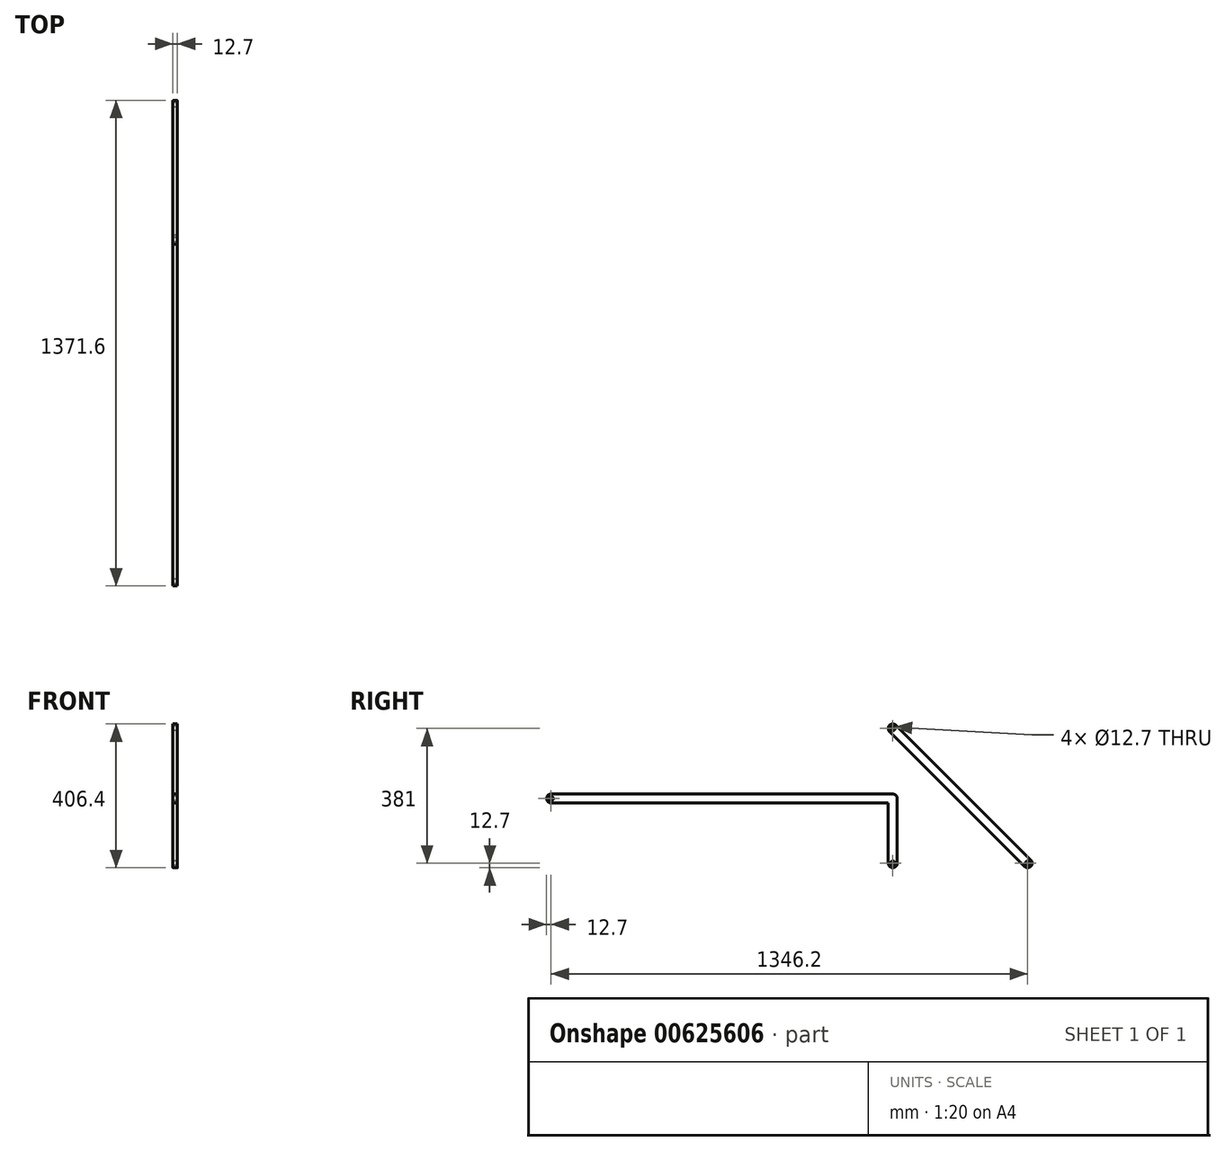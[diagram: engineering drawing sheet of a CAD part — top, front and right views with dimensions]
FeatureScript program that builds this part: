
annotation { "Feature Type Name" : "Feature", "Feature Type Description" : "" }
export const myFeature = defineFeature(function(context is Context, id is Id, definition is map)
    precondition{}
    {
        {
            var Q0;
            Q0=qCreatedBy(makeId("Right.planeOp"),FACE);
            var sketch = newSketch(context, id + "F0", { "sketchPlane" : qUnion([Q0])});
            skLineSegment(sketch, "E0", {"start": v(0, 0) * mm, "end": v(0, -381) * mm, "construction": true});
            skLineSegment(sketch, "E1", {"start": v(0, -381) * mm, "end": v(381, -381) * mm, "construction": true});
            skLineSegment(sketch, "E2", {"start": v(381, -381) * mm, "end": v(0, 0) * mm, "construction": true});
            skCircle(sketch, "E3", {"center": v(0, 0) * mm, "radius": 6.35 * mm});
            skCircle(sketch, "E4", {"center": v(381, -381) * mm, "radius": 6.35 * mm});
            skCircle(sketch, "E5", {"center": v(0, -381) * mm, "radius": 6.35 * mm});
            skArc(sketch, "E6.0.startCap", {"start": v(389.98, -372.02) * mm, "mid": v(389.98, -389.98) * mm, "end": v(372.02, -389.98) * mm});
            skArc(sketch, "E6.0.endCap", {"start": v(-8.98, -8.98) * mm, "mid": v(-8.98, 8.98) * mm, "end": v(8.98, 8.98) * mm});
            skLineSegment(sketch, "E6.0.left", {"start": v(372.02, -389.98) * mm, "end": v(-8.98, -8.98) * mm});
            skLineSegment(sketch, "E6.0.right", {"start": v(389.98, -372.02) * mm, "end": v(8.98, 8.98) * mm});
            skArc(sketch, "E6.1.startCap", {"start": v(-12.7, 0) * mm, "mid": v(0, 12.7) * mm, "end": v(12.7, 0) * mm, "construction": true});
            skArc(sketch, "E6.1.endCap", {"start": v(12.7, -381) * mm, "mid": v(0, -393.7) * mm, "end": v(-12.7, -381) * mm});
            skLineSegment(sketch, "E6.1.left", {"start": v(12.7, 0) * mm, "end": v(12.7, -381) * mm});
            skLineSegment(sketch, "E6.1.right", {"start": v(-12.7, 0) * mm, "end": v(-12.7, -381) * mm});
            skArc(sketch, "E6.2.startCap", {"start": v(0, -393.7) * mm, "mid": v(-12.7, -381) * mm, "end": v(0, -368.3) * mm});
            skArc(sketch, "E6.2.endCap", {"start": v(381, -368.3) * mm, "mid": v(393.7, -381) * mm, "end": v(381, -393.7) * mm});
            skLineSegment(sketch, "E6.2.left", {"start": v(0, -368.3) * mm, "end": v(381, -368.3) * mm});
            skLineSegment(sketch, "E6.2.right", {"start": v(0, -393.7) * mm, "end": v(381, -393.7) * mm});
            skLineSegment(sketch, "E7", {"start": v(0, -198.12) * mm, "end": v(-965.2, -198.12) * mm, "construction": true});
            skCircle(sketch, "E8", {"center": v(-965.2, -198.12) * mm, "radius": 6.35 * mm});
            skArc(sketch, "E9.0.startCap", {"start": v(0, -185.42) * mm, "mid": v(12.7, -198.12) * mm, "end": v(0, -210.82) * mm});
            skArc(sketch, "E9.0.endCap", {"start": v(-965.2, -210.82) * mm, "mid": v(-977.9, -198.12) * mm, "end": v(-965.2, -185.42) * mm});
            skLineSegment(sketch, "E9.0.left", {"start": v(0, -210.82) * mm, "end": v(-965.2, -210.82) * mm});
            skLineSegment(sketch, "E9.0.right", {"start": v(0, -185.42) * mm, "end": v(-965.2, -185.42) * mm});
            skSolve(sketch);
        }
        {
            var Q0;
            {var subQ5=sQuery(id+"F0.wireOp",EDGE,"E6.1.right");Q0=makeQuery(id+"F0.imprint","IMPRINT",FACE,{"disambiguationData":[TD([[makeQuery(id+"F0.imprint","IMPRINT",EDGE,{"derivedFrom":subQ5}),1.0]])]});}
            var Q1;
            {var subQ5=sQuery(id+"F0.wireOp",EDGE,"E6.0.startCap");Q1=makeQuery(id+"F0.imprint","IMPRINT",FACE,{"disambiguationData":[TD([[makeQuery(id+"F0.imprint","IMPRINT",EDGE,{"derivedFrom":subQ5}),1.0]])]});}
            var Q2;
            Q2=makeQuery(id+"F0.imprint","IMPRINT",FACE,{"disambiguationData":[TD([[makeQuery(id+"F0.imprint","IMPRINT",EDGE,{"derivedFrom":sQuery(id+"F0.wireOp",EDGE,"E4")}),-1.0]])]});
            var Q3;
            Q3=makeQuery(id+"F0.imprint","IMPRINT",FACE,{"disambiguationData":[TD([[makeQuery(id+"F0.imprint","IMPRINT",EDGE,{"derivedFrom":sQuery(id+"F0.wireOp",EDGE,"E3")}),-1.0]])]});
            var Q4;
            Q4=makeQuery(id+"F0.imprint","IMPRINT",FACE,{"disambiguationData":[TD([[makeQuery(id+"F0.imprint","IMPRINT",EDGE,{"derivedFrom":sQuery(id+"F0.wireOp",EDGE,"E5")}),-1.0]])]});
            var Q5;
            {var subQ1=sQuery(id+"F0.wireOp",EDGE,"E6.0.left");var subQ5=sQuery(id+"F0.wireOp",EDGE,"E6.0.endCap");var subQ6=makeQuery(id+"F0.imprint","INTERSECT",VERTEX,{"derivedFrom":[subQ5,subQ1]});Q5=makeQuery(id+"F0.imprint","IMPRINT",FACE,{"disambiguationData":[TD([[makeQuery(id+"F0.imprint","IMPRINT",EDGE,{"disambiguationData":[TD([[subQ6,-1.0]])],"derivedFrom":subQ5}),1.0]])]});}
            var Q6;
            Q6=makeQuery(id+"F0.imprint","IMPRINT",FACE,{"disambiguationData":[TD([[makeQuery(id+"F0.imprint","IMPRINT",EDGE,{"derivedFrom":sQuery(id+"F0.wireOp",EDGE,"E8")}),-1.0]])]});
            var Q7;
            {var subQ6=sQuery(id+"F0.wireOp",EDGE,"E9.0.startCap");var subQ9=sQuery(id+"F0.wireOp",EDGE,"E6.1.left");var subQ11=makeQuery(id+"F0.imprint","INTERSECT",VERTEX,{"derivedFrom":[subQ9,subQ6]});Q7=makeQuery(id+"F0.imprint","IMPRINT",FACE,{"disambiguationData":[TD([[makeQuery(id+"F0.imprint","IMPRINT",EDGE,{"disambiguationData":[TD([[subQ11,-1.0]])],"derivedFrom":subQ9}),-1.0]])]});}
            extrude(context, id + "F1", {"entities" : qUnion([Q0, Q1, Q2, Q3, Q4, Q5, Q6, Q7]), "depth" : 12.7 * mm, "offsetDistance" : 25.4 * mm});
        }
    });
